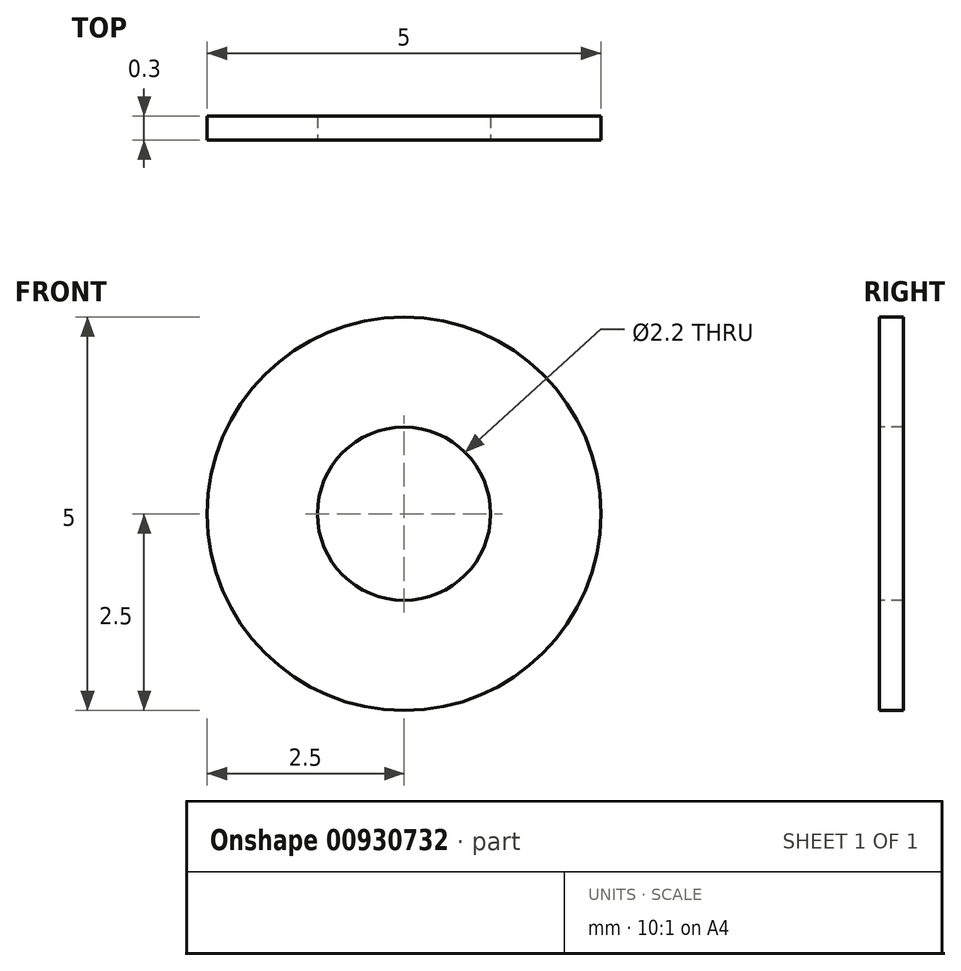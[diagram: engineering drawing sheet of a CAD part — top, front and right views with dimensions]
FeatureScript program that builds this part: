
annotation { "Feature Type Name" : "Feature", "Feature Type Description" : "" }
export const myFeature = defineFeature(function(context is Context, id is Id, definition is map)
    precondition{}
    {
        {
            var Q0;
            Q0=qCreatedBy(makeId("Front.planeOp"),FACE);
            var sketch = newSketch(context, id + "F0", { "sketchPlane" : qUnion([Q0])});
            skCircle(sketch, "E0", {"center": v(0, 0) * mm, "radius": 1.1 * mm});
            skCircle(sketch, "E1", {"center": v(0, 0) * mm, "radius": 2.5 * mm});
            skSolve(sketch);
        }
        {
            var Q0;
            Q0 = qSketchRegion(id + "F0", true);
            extrude(context, id + "F1", {"entities" : qUnion([Q0]), "oppositeDirection" : true, "depth" : 0.3 * mm, "offsetDistance" : 25 * mm});
        }
    });
